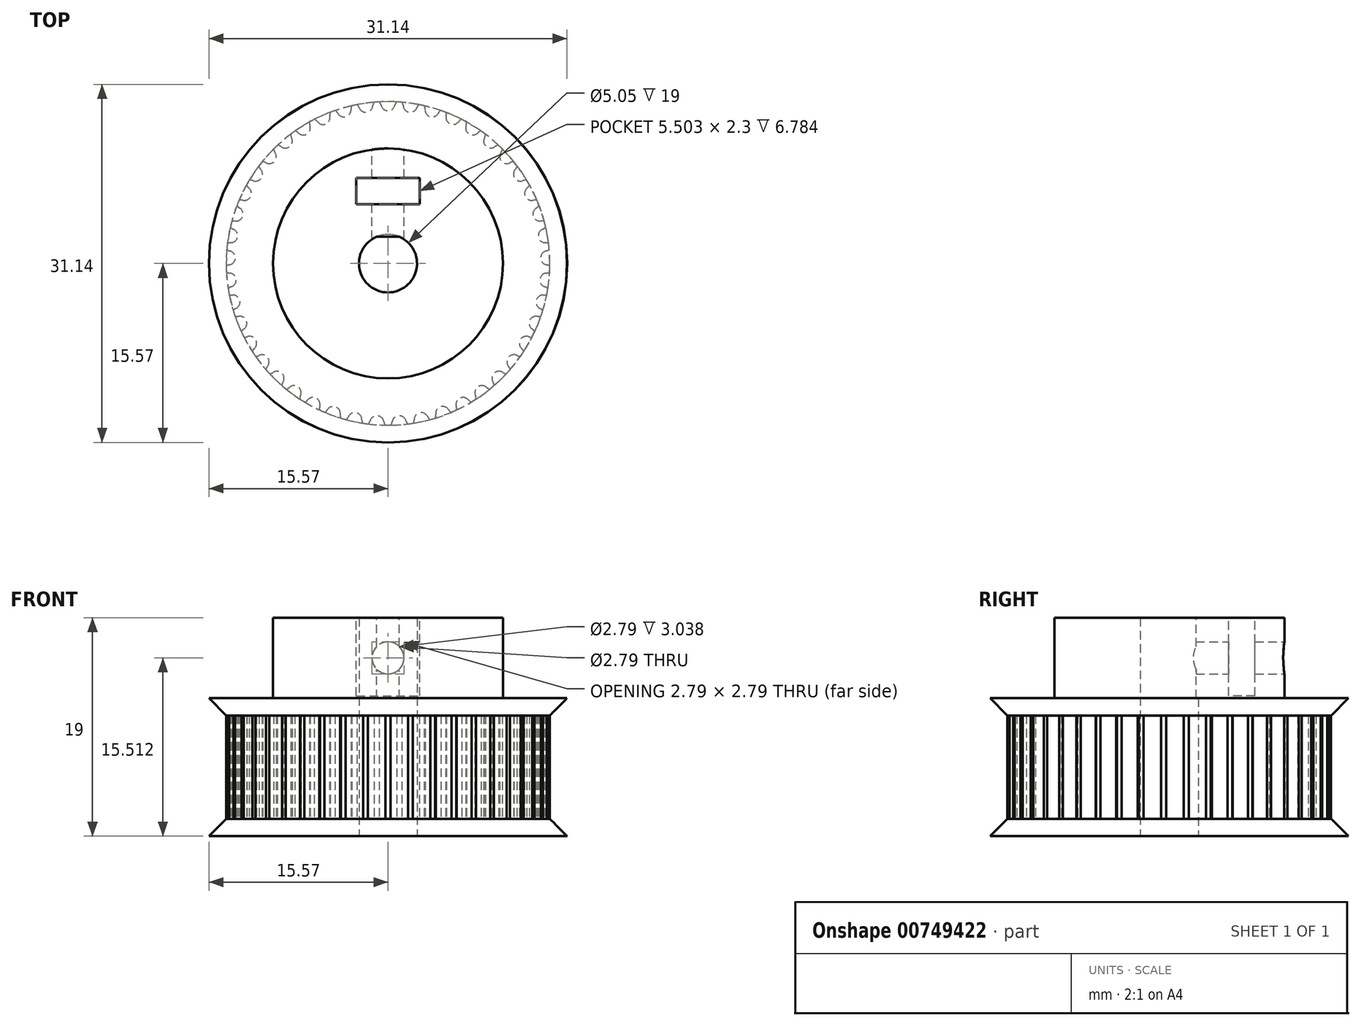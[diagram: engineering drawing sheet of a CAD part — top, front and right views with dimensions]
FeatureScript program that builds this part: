
annotation { "Feature Type Name" : "Feature", "Feature Type Description" : "" }
export const myFeature = defineFeature(function(context is Context, id is Id, definition is map)
    precondition{}
    {
        {
            assignVariable(context, id + "F0", {"name" : "Teeth", "anyValue" : 45});
        }
        {
            var Q0;
            Q0=qCreatedBy(makeId("Top.planeOp"),FACE);
            var sketch = newSketch(context, id + "F1", { "sketchPlane" : qUnion([Q0])});
            skCircle(sketch, "E0", {"center": v(0, 0) * mm, "radius": 14.07 * mm});
            skSolve(sketch);
        }
        {
            var Q0;
            Q0=qCreatedBy(makeId("Top.planeOp"),FACE);
            var sketch = newSketch(context, id + "F2", { "sketchPlane" : qUnion([Q0])});
            skArc(sketch, "E1.0", {"start": v(0.77, 14.05) * mm, "mid": v(0, 14.07) * mm, "end": v(-0.77, 14.05) * mm});
            skLineSegment(sketch, "E2", {"start": v(0, 0) * mm, "end": v(0, 13.9) * mm, "construction": true});
            skArc(sketch, "E3", {"start": v(0, 13.28) * mm, "mid": v(-0.38, 13.42) * mm, "end": v(-0.6, 13.76) * mm});
            skArc(sketch, "E4", {"start": v(-0.6, 13.76) * mm, "mid": v(-0.63, 13.87) * mm, "end": v(-0.68, 13.96) * mm});
            skArc(sketch, "E5", {"start": v(-0.68, 13.96) * mm, "mid": v(-0.71, 14.01) * mm, "end": v(-0.77, 14.05) * mm});
            skArc(sketch, "E6.MirrorCS", {"start": v(0, 13.28) * mm, "mid": v(0.38, 13.42) * mm, "end": v(0.6, 13.76) * mm});
            skArc(sketch, "E7.MirrorCS", {"start": v(0.68, 13.96) * mm, "mid": v(0.71, 14.01) * mm, "end": v(0.77, 14.05) * mm});
            skArc(sketch, "E8.MirrorCS", {"start": v(0.6, 13.76) * mm, "mid": v(0.63, 13.87) * mm, "end": v(0.68, 13.96) * mm});
            skSolve(sketch);
        }
        {
            var Q0;
            Q0=qSketchRegion(id+"F1",true);
            extrude(context, id + "F3", {"entities" : qUnion([Q0]), "depth" : 9 * mm, "offsetDistance" : 25 * mm});
        }
        {
            var Q0;
            Q0=makeQuery(id+"F2.imprint","IMPRINT",FACE,{"disambiguationData":[TD([[makeQuery(id+"F2.imprint","IMPRINT",EDGE,{"derivedFrom":sQuery(id+"F2.wireOp",EDGE,"E1.0")}),1.0]])]});
            extrude(context, id + "F4", {"entities" : qUnion([Q0]), "depth" : 25 * mm, "offsetDistance" : 25 * mm});
        }
        {
            var Q0;
            Q0=makeQuery(id+"F4.opExtrude","SWEPT_BODY",BODY,{"disambiguationData":[OSD([sQuery(id+"F2.wireOp",EDGE,"E1.0"),sQuery(id+"F2.wireOp",EDGE,"E3"),sQuery(id+"F2.wireOp",EDGE,"E4"),sQuery(id+"F2.wireOp",EDGE,"E5"),sQuery(id+"F2.wireOp",EDGE,"E6.MirrorCS"),sQuery(id+"F2.wireOp",EDGE,"E7.MirrorCS"),sQuery(id+"F2.wireOp",EDGE,"E8.MirrorCS")])]});
            var Q1;
            Q1=sQuery(id+"F1.wireOp",EDGE,"E0");
            circularPattern(context, id + "F5", {"operationType" : NewBodyOperationType.REMOVE, "entities" : qUnion([Q0]), "axis" : qUnion([Q1]), "angle" : 360 * degree, "instanceCount" : getVariable(context, 'Teeth'), "equalSpace" : true});
        }
        {
            var Q0;
            Q0=makeQuery(id+"F3.opExtrude","CAP_FACE",FACE,{"disambiguationData":[OSD([sQuery(id+"F1.wireOp",EDGE,"E0")])],"isStart":false});
            var sketch = newSketch(context, id + "F6", { "sketchPlane" : qUnion([Q0])});
            skCircle(sketch, "E9", {"center": v(0, 0) * mm, "radius": 10 * mm});
            skSolve(sketch);
        }
        {
            var Q0;
            Q0=makeQuery(id+"F6.imprint","IMPRINT",FACE,{"disambiguationData":[TD([[makeQuery(id+"F6.imprint","IMPRINT",EDGE,{"derivedFrom":sQuery(id+"F6.wireOp",EDGE,"E9")}),-1.0]])]});
            var sketch = newSketch(context, id + "F7", { "sketchPlane" : qUnion([Q0])});
            skCircle(sketch, "E10.0", {"center": v(0, 0) * mm, "radius": 14.07 * mm});
            skSolve(sketch);
        }
        {
            var Q0;
            Q0=qSketchRegion(id+"F7",true);
            extrude(context, id + "F8", {"entities" : qUnion([Q0]), "operationType" : NewBodyOperationType.ADD, "depth" : 1.5 * mm, "offsetDistance" : 25 * mm, "hasDraft" : true, "draftAngle" : 45 * degree});
        }
        {
            var Q0;
            Q0=qSketchRegion(id+"F6",true);
            extrude(context, id + "F9", {"entities" : qUnion([Q0]), "operationType" : NewBodyOperationType.ADD, "depth" : 8.5 * mm, "offsetDistance" : 25 * mm});
        }
        {
            var Q0;
            Q0=qCreatedBy(makeId("Top.planeOp"),FACE);
            var sketch = newSketch(context, id + "F10", { "sketchPlane" : qUnion([Q0])});
            skCircle(sketch, "E11", {"center": v(0, 0) * mm, "radius": 2.52 * mm});
            skSolve(sketch);
        }
        {
            var Q0;
            Q0=qCreatedBy(makeId("Top.planeOp"),FACE);
            var sketch = newSketch(context, id + "F11", { "sketchPlane" : qUnion([Q0])});
            skCircle(sketch, "E12.0", {"center": v(0, 0) * mm, "radius": 2.6 * mm});
            skSolve(sketch);
        }
        {
            var Q0;
            Q0=makeQuery(id+"F9.opExtrude","CAP_FACE",FACE,{"disambiguationData":[OSD([sQuery(id+"F6.wireOp",EDGE,"E9")])],"isStart":false});
            var sketch = newSketch(context, id + "F12", { "sketchPlane" : qUnion([Q0])});
            skLineSegment(sketch, "E13", {"start": v(0, 10) * mm, "end": v(0, 7.44) * mm, "construction": true});
            skLineSegment(sketch, "E14.bottom", {"start": v(-2.75, 7.44) * mm, "end": v(2.75, 7.44) * mm});
            skLineSegment(sketch, "E14.top", {"start": v(-2.75, 7.44) * mm, "end": v(2.75, 7.44) * mm});
            skLineSegment(sketch, "E14.left", {"start": v(-2.75, 7.44) * mm, "end": v(-2.75, 7.44) * mm});
            skLineSegment(sketch, "E14.right", {"start": v(2.75, 7.44) * mm, "end": v(2.75, 7.44) * mm});
            skPoint(sketch, "E14.middle", {"position": v(0, 7.44) * mm});
            skLineSegment(sketch, "E15.top", {"start": v(-2.75, 5.14) * mm, "end": v(2.75, 5.14) * mm});
            skLineSegment(sketch, "E15.left", {"start": v(-2.75, 7.44) * mm, "end": v(-2.75, 5.14) * mm});
            skLineSegment(sketch, "E15.right", {"start": v(2.75, 7.44) * mm, "end": v(2.75, 5.14) * mm});
            skSolve(sketch);
        }
        {
            var Q0;
            Q0=qSketchRegion(id+"F12",true);
            extrude(context, id + "F13", {"entities" : qUnion([Q0]), "operationType" : NewBodyOperationType.REMOVE, "oppositeDirection" : true, "depth" : 6.78 * mm, "offsetDistance" : 25 * mm});
        }
        {
            var Q0;
            Q0=makeQuery(id+"F13.boolean.opBoolean","COPY",FACE,{"derivedFrom":makeQuery(id+"F13.opExtrude","SWEPT_FACE",FACE,{"disambiguationData":[OSD([sQuery(id+"F12.wireOp",EDGE,"E15.top")])]})});
            var sketch = newSketch(context, id + "F14", { "sketchPlane" : qUnion([Q0])});
            skLineSegment(sketch, "E16", {"start": v(0, 17.5) * mm, "end": v(0, 15.4) * mm, "construction": true});
            skLineSegment(sketch, "E17", {"start": v(0, 15.4) * mm, "end": v(0, 12.62) * mm, "construction": true});
            skCircle(sketch, "E18", {"center": v(0, 14.01) * mm, "radius": 1.4 * mm});
            skSolve(sketch);
        }
        {
            var Q0;
            Q0=makeQuery(id+"F11.imprint","IMPRINT",FACE,{"disambiguationData":[TD([[makeQuery(id+"F11.imprint","IMPRINT",EDGE,{"derivedFrom":sQuery(id+"F11.wireOp",EDGE,"E12.0")}),1.0]])]});
            var sketch = newSketch(context, id + "F15", { "sketchPlane" : qUnion([Q0])});
            skCircle(sketch, "E19", {"center": v(0, 0) * mm, "radius": 14.07 * mm});
            skSolve(sketch);
        }
        {
            var Q0;
            Q0=qSketchRegion(id+"F15",true);
            extrude(context, id + "F16", {"entities" : qUnion([Q0]), "operationType" : NewBodyOperationType.ADD, "oppositeDirection" : true, "depth" : 1.5 * mm, "offsetDistance" : 25 * mm, "hasDraft" : true, "draftAngle" : 45 * degree});
        }
        {
            var Q0;
            Q0=qSketchRegion(id+"F10",true);
            var Q1;
            Q1=sQuery(id+"F10.wireOp",EDGE,"E11");
            extrude(context, id + "F17", {"entities" : qUnion([Q0]), "operationType" : NewBodyOperationType.REMOVE, "surfaceEntities" : qUnion([Q1]), "depth" : 25 * mm, "offsetDistance" : 25 * mm, "hasSecondDirection" : true, "secondDirectionOppositeDirection" : true, "secondDirectionDepth" : 25 * mm});
        }
        {
            var Q0;
            Q0=makeQuery(id+"F9.opExtrude","CAP_FACE",FACE,{"disambiguationData":[OSD([sQuery(id+"F6.wireOp",EDGE,"E9")])],"isStart":false});
            var sketch = newSketch(context, id + "F18", { "sketchPlane" : qUnion([Q0])});
            skCircle(sketch, "E20", {"center": v(0, 0) * mm, "radius": 2.33 * mm, "construction": true});
            skCircle(sketch, "E21.0", {"center": v(0, 0) * mm, "radius": 2.52 * mm, "construction": true});
            skArc(sketch, "E22", {"start": v(0, -2.52) * mm, "mid": v(0.5, 2.47) * mm, "end": v(-0.98, -2.33) * mm});
            skLineSegment(sketch, "E23", {"start": v(0, 2.33) * mm, "end": v(-0.98, 2.33) * mm});
            skLineSegment(sketch, "E24", {"start": v(0, 2.33) * mm, "end": v(0.98, 2.33) * mm});
            skArc(sketch, "E25", {"start": v(-0.98, 2.32) * mm, "mid": v(0.5, -2.47) * mm, "end": v(0, 2.52) * mm});
            skSolve(sketch);
        }
        {
            var Q0;
            {var subQ0=sQuery(id+"F18.wireOp",EDGE,"E22");Q0=makeQuery(id+"F18.imprint","IMPRINT",FACE,{"disambiguationData":[TD([[makeQuery(id+"F18.imprint","IMPRINT",EDGE,{"derivedFrom":subQ0}),-1.0]])]});}
            var Q1;
            Q1=makeQuery(id+"F8.opExtrude","CAP_FACE",FACE,{"disambiguationData":[OSD([sQuery(id+"F7.wireOp",EDGE,"E10.0")])],"isStart":false});
            var Q2;
            Q2=makeQuery(id+"F16.opExtrude","CAP_FACE",FACE,{"disambiguationData":[OSD([sQuery(id+"F15.wireOp",EDGE,"E19")])],"isStart":false});
            extrude(context, id + "F19", {"entities" : qUnion([Q0]), "operationType" : NewBodyOperationType.ADD, "endBound" : BoundingType.UP_TO_SURFACE, "oppositeDirection" : true, "depth" : 25 * mm, "endBoundEntityFace" : qUnion([Q1]), "offsetDistance" : 5 * mm});
        }
        {
            var Q0;
            Q0=makeQuery(id+"F14.imprint","IMPRINT",FACE,{"disambiguationData":[TD([[makeQuery(id+"F14.imprint","IMPRINT",EDGE,{"derivedFrom":sQuery(id+"F14.wireOp",EDGE,"E18")}),1.0]])]});
            extrude(context, id + "F20", {"entities" : qUnion([Q0]), "operationType" : NewBodyOperationType.REMOVE, "oppositeDirection" : true, "depth" : 5 * mm, "offsetDistance" : 25 * mm, "hasSecondDirection" : true, "secondDirectionOppositeDirection" : false, "secondDirectionDepth" : 15 * mm});
        }
    });
